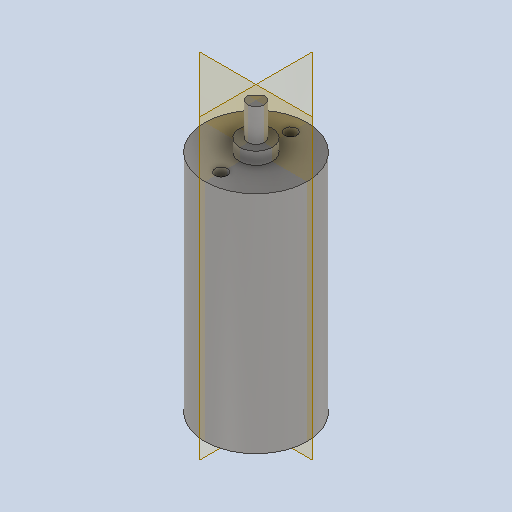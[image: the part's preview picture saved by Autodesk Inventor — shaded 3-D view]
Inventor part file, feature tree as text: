
AUTODESK INVENTOR PART (.ipt)
format: ipt  version: 2022.6 (Build 266554000, 554)  size: 123,904 bytes
history: native  units: mm
features: sketch x4, extrude x3, projected_geometry x2, hole x1
ambient origin geometry x8: Origin, YZ Plane, XZ Plane, XY Plane, X Axis, Y Axis, Z Axis, Center Point
bodies: Solid1 (feature_tree)
feature tree (10):
  extrude  "Extrusion1"  Depth=55.0mm TaperAngle=0.0deg
  extrude  "Extrusion2"  Depth=3.0mm TaperAngle=0.0deg
  extrude  "Extrusion3"  Depth=3.0mm
  hole  "Hole1"  [1 undecoded]
  sketch  "Sketch1"  dims[d0=25.0mm d1=55.0mm d2=0.0mm]
  sketch  "Sketch2"  dims[d3=8.0mm d4=3.0mm d5=0.0mm]
  projected_geometry  "Projected Loop1"
  sketch  "Sketch3"  dims[d6=4.0mm d7=3.0mm]
  sketch  "Sketch4"  dims[d8=8.0mm d9=0.0mm d10=17.0mm d11=3.0mm d12=6.0mm d13=4.0mm d14=2.0mm d15=90.0deg d16=8.0mm d17=20.594885mm]
  projected_geometry  "Projected Loop2"
note: 1 required parameter value undecoded (feature->parameter linkage not recoverable at this tier; creation-order binding heuristic only, values carry confidence <= 0.55)
